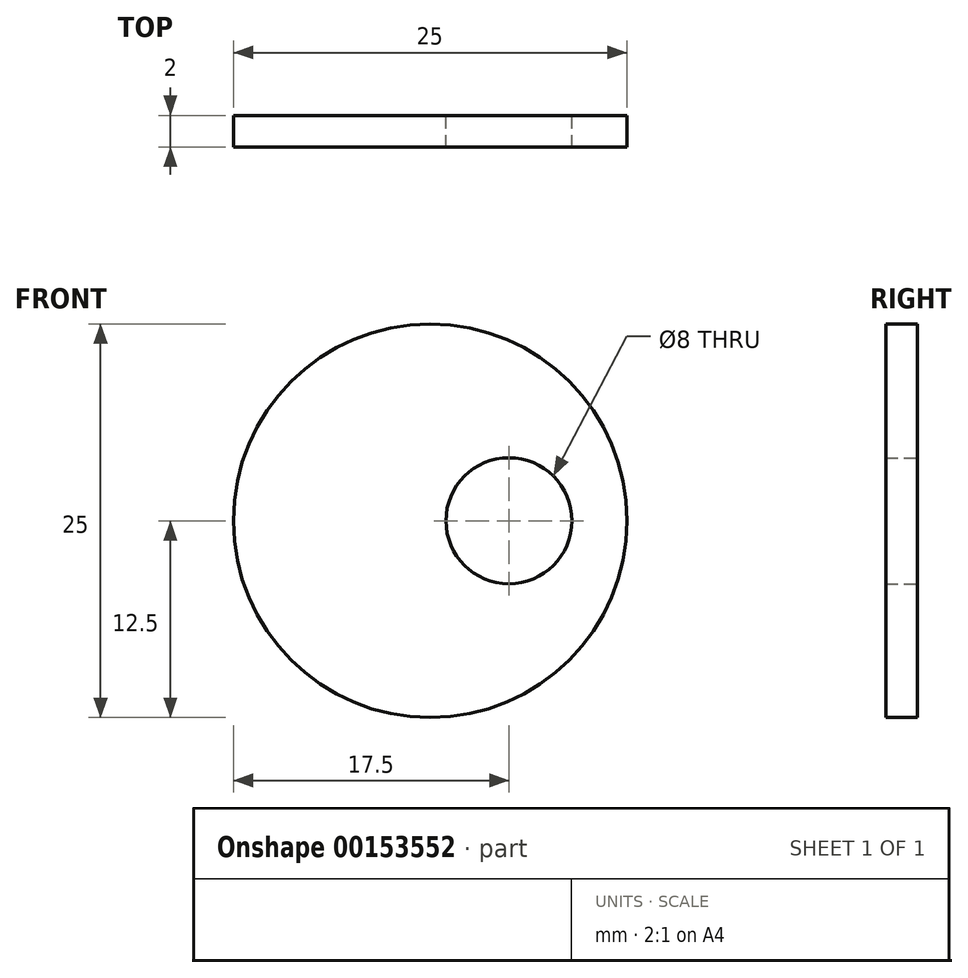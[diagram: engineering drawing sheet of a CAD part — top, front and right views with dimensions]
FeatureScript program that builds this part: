
annotation { "Feature Type Name" : "Feature", "Feature Type Description" : "" }
export const myFeature = defineFeature(function(context is Context, id is Id, definition is map)
    precondition{}
    {
        {
            var Q0;
            Q0=qCreatedBy(makeId("Front.planeOp"),FACE);
            var sketch = newSketch(context, id + "F0", { "sketchPlane" : qUnion([Q0])});
            skCircle(sketch, "E0", {"center": v(0, 0) * mm, "radius": 5 * mm, "construction": true});
            skCircle(sketch, "E1", {"center": v(0, 0) * mm, "radius": 12.5 * mm});
            skCircle(sketch, "E2", {"center": v(5, 0) * mm, "radius": 4 * mm});
            skLineSegment(sketch, "E3", {"start": v(0, 0) * mm, "end": v(5, 0) * mm, "construction": true});
            skSolve(sketch);
        }
        {
            var Q0;
            Q0 = qSketchRegion(id + "F0", true);
            var Q1;
            Q1 = qConstructionFilter(qBodyType(qCreatedBy(id + "F0" ,EDGE), BodyType.WIRE), ConstructionObject.NO);
            extrude(context, id + "F1", {"entities" : qUnion([Q0]), "surfaceEntities" : qUnion([Q1]), "depth" : 2 * mm});
        }
    });
